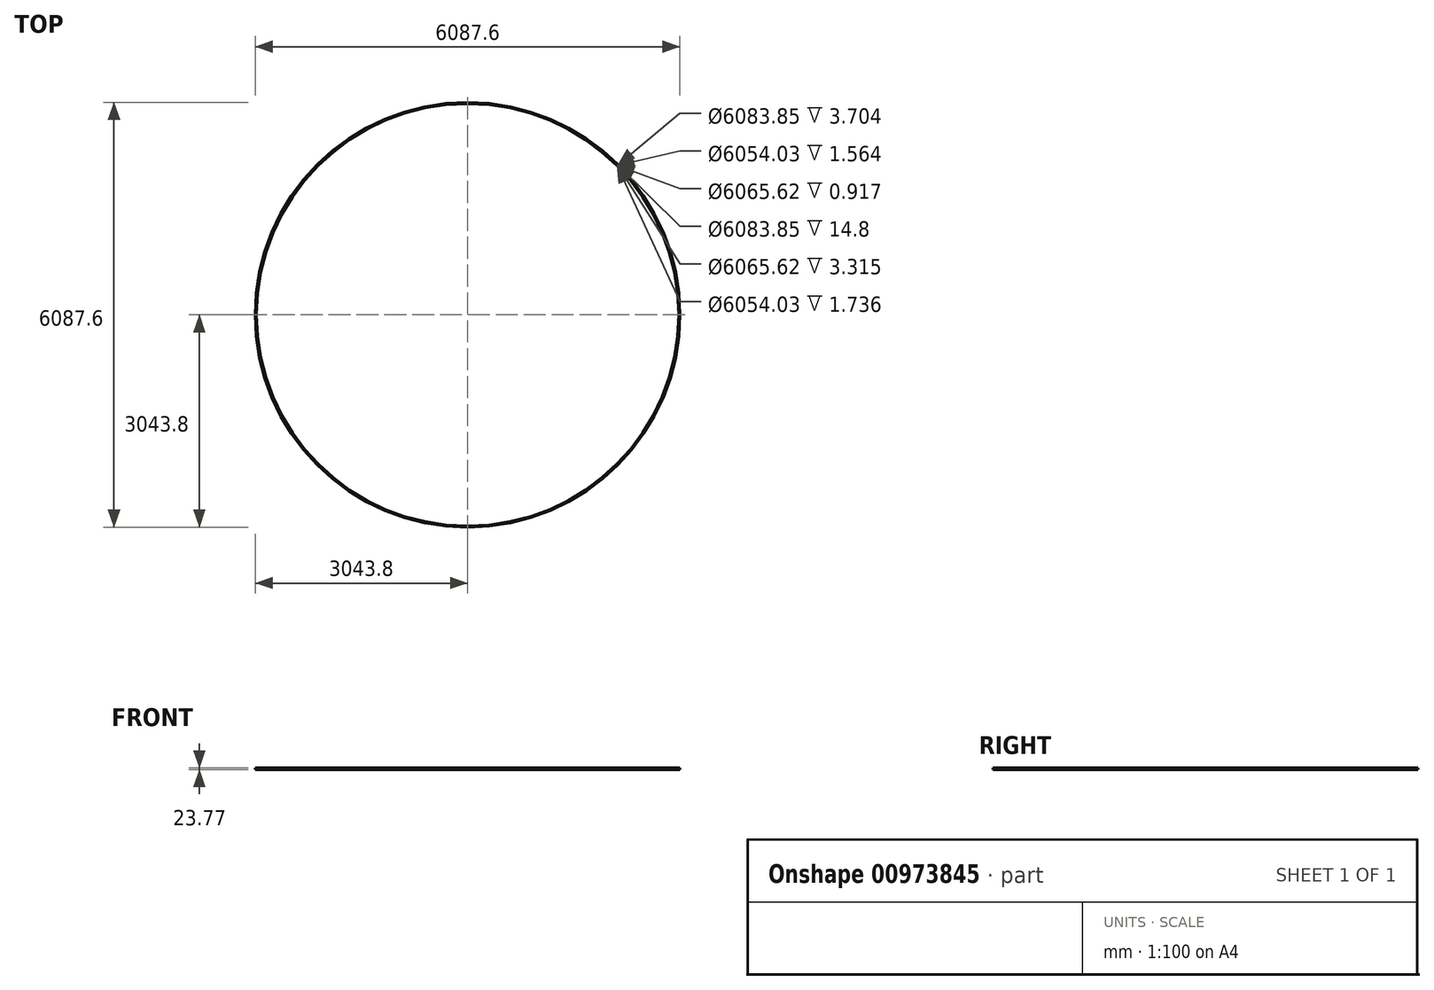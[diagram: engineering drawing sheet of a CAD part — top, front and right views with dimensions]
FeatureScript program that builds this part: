
annotation { "Feature Type Name" : "Feature", "Feature Type Description" : "" }
export const myFeature = defineFeature(function(context is Context, id is Id, definition is map)
    precondition{}
    {
        {
            var Q0;
            Q0=qCreatedBy(makeId("Front.planeOp"),FACE);
            var sketch = newSketch(context, id + "F0", { "sketchPlane" : qUnion([Q0])});
            skLineSegment(sketch, "E0", {"start": v(0, 11.38) * mm, "end": v(0, -12.39) * mm});
            skLineSegment(sketch, "E1.MirrorCS", {"start": v(9.34, 3.46) * mm, "end": v(9.34, 4.38) * mm});
            skLineSegment(sketch, "E2.MirrorCS", {"start": v(11, 4.38) * mm, "end": v(11, 3.46) * mm});
            skLineSegment(sketch, "E3.MirrorCS", {"start": v(1.88, 4.38) * mm, "end": v(1.88, -10.42) * mm});
            skLineSegment(sketch, "E4.MirrorCS", {"start": v(1.88, -10.42) * mm, "end": v(9.34, -10.42) * mm});
            skLineSegment(sketch, "E5.MirrorCS", {"start": v(9.34, -9.07) * mm, "end": v(11, -9.07) * mm});
            skLineSegment(sketch, "E6.MirrorCS", {"start": v(0, 11.38) * mm, "end": v(16.8, 11.38) * mm});
            skLineSegment(sketch, "E7.MirrorCS", {"start": v(16.8, 4.38) * mm, "end": v(11, 4.38) * mm});
            skLineSegment(sketch, "E8.MirrorCS", {"start": v(16.8, 11.38) * mm, "end": v(16.8, 9.65) * mm});
            skLineSegment(sketch, "E9.MirrorCS", {"start": v(11, 3.46) * mm, "end": v(9.34, 3.46) * mm});
            skLineSegment(sketch, "E10.MirrorCS", {"start": v(1.88, 7.54) * mm, "end": v(1.88, 5.94) * mm});
            skLineSegment(sketch, "E11.MirrorCS", {"start": v(11, -9.07) * mm, "end": v(11, -10.42) * mm});
            skLineSegment(sketch, "E12.MirrorCS", {"start": v(9.34, 4.38) * mm, "end": v(1.88, 4.38) * mm});
            skLineSegment(sketch, "E13.MirrorCS", {"start": v(16.8, 5.94) * mm, "end": v(16.8, 4.38) * mm});
            skLineSegment(sketch, "E14.MirrorCS", {"start": v(1.88, 5.94) * mm, "end": v(16.8, 5.94) * mm});
            skLineSegment(sketch, "E15.MirrorCS", {"start": v(16.8, 9.65) * mm, "end": v(1.88, 9.65) * mm});
            skPoint(sketch, "E16.MirrorP", {"position": v(9.34, 7.54) * mm});
            skLineSegment(sketch, "E17.MirrorCS", {"start": v(1.88, 9.65) * mm, "end": v(1.88, 7.54) * mm});
            skLineSegment(sketch, "E18.MirrorCS", {"start": v(11, -10.42) * mm, "end": v(11, -12.39) * mm});
            skLineSegment(sketch, "E19.MirrorCS", {"start": v(11, -12.39) * mm, "end": v(0, -12.39) * mm});
            skLineSegment(sketch, "E20.MirrorCS", {"start": v(9.34, -10.42) * mm, "end": v(9.34, -9.07) * mm});
            skSolve(sketch);
        }
        {
            var Q0;
            Q0=qCreatedBy(makeId("Top.planeOp"),FACE);
            var sketch = newSketch(context, id + "F1", { "sketchPlane" : qUnion([Q0])});
            skCircle(sketch, "E21", {"center": v(3043.8, 0) * mm, "radius": 3045 * mm});
            skSolve(sketch);
        }
        {
            var Q0;
            Q0=makeQuery(id+"F0.imprint","IMPRINT",FACE,{"disambiguationData":[TD([[makeQuery(id+"F0.imprint","IMPRINT",EDGE,{"derivedFrom":sQuery(id+"F0.wireOp",EDGE,"E0")}),1.0]])]});
            var Q1;
            Q1=sQuery(id+"F1.wireOp",EDGE,"E21");
            sweep(context, id + "F2", {"profiles" : qUnion([Q0]), "path" : qUnion([Q1])});
        }
    });
